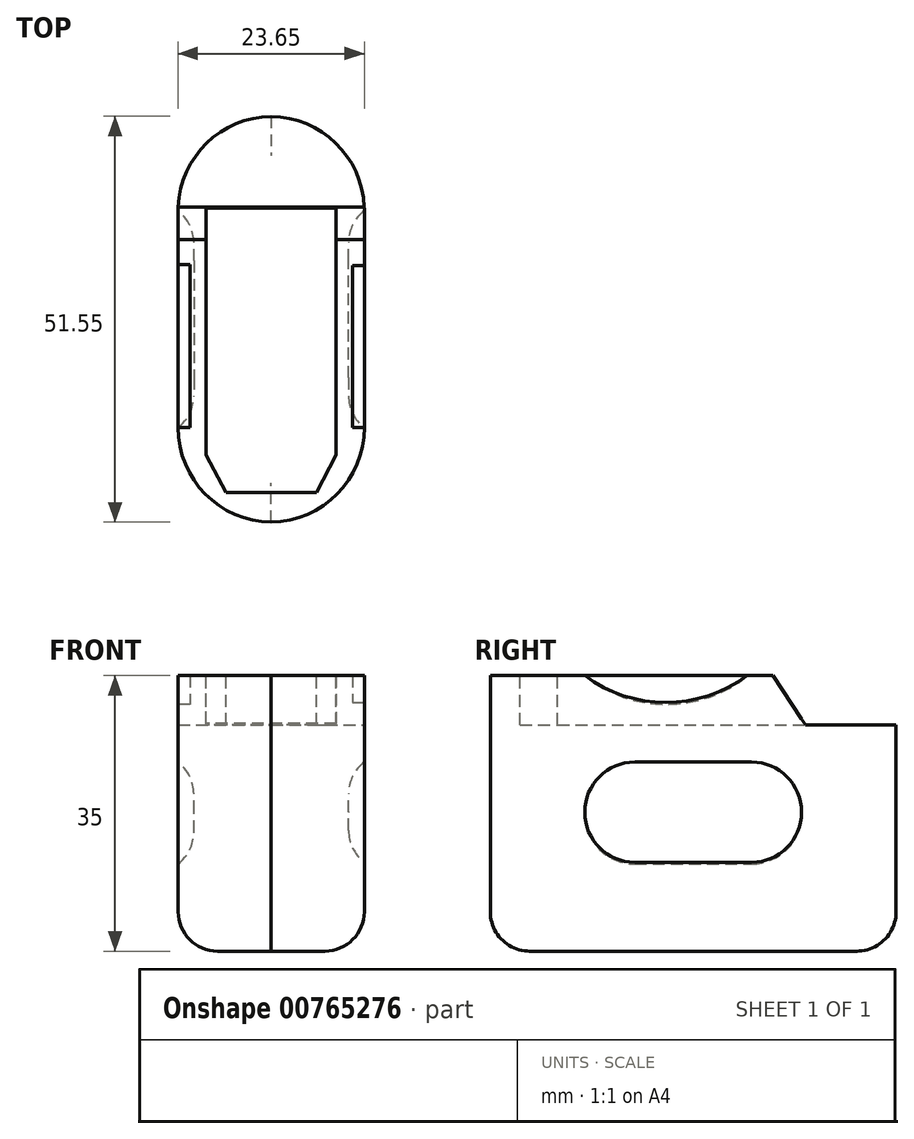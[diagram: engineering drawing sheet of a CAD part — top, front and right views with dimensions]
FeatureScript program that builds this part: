
annotation { "Feature Type Name" : "Feature", "Feature Type Description" : "" }
export const myFeature = defineFeature(function(context is Context, id is Id, definition is map)
    precondition{}
    {
        {
            var Q0;
            Q0=qCreatedBy(makeId("Top.planeOp"),FACE);
            var sketch = newSketch(context, id + "F0", { "sketchPlane" : qUnion([Q0])});
            skLineSegment(sketch, "E0", {"start": v(-11.06, 0) * mm, "end": v(-11.06, -51.55) * mm});
            skLineSegment(sketch, "E1", {"start": v(-11.06, -51.55) * mm, "end": v(12.59, -51.55) * mm});
            skLineSegment(sketch, "E2", {"start": v(12.59, -51.55) * mm, "end": v(12.59, 0) * mm});
            skLineSegment(sketch, "E3", {"start": v(-11.06, 0) * mm, "end": v(12.59, 0) * mm});
            skSolve(sketch);
        }
        {
            var Q0;
            Q0 = qSketchRegion(id + "F0", true);
            extrude(context, id + "F1", {"entities" : qUnion([Q0]), "depth" : 35 * mm, "offsetDistance" : 25.4 * mm});
        }
        {
            var Q0;
            Q0=makeQuery(id+"F1.opExtrude","SWEPT_FACE",FACE,{"disambiguationData":[OSD([sQuery(id+"F0.wireOp",EDGE,"E2")])]});
            var sketch = newSketch(context, id + "F2", { "sketchPlane" : qUnion([Q0])});
            skLineSegment(sketch, "E4", {"start": v(0, 35) * mm, "end": v(0, 28.75) * mm});
            skLineSegment(sketch, "E5", {"start": v(-11.5, 28.75) * mm, "end": v(-15.66, 35) * mm});
            skLineSegment(sketch, "E6", {"start": v(-11.5, 28.75) * mm, "end": v(0, 28.75) * mm});
            skLineSegment(sketch, "E7", {"start": v(0, 35) * mm, "end": v(-15.66, 35) * mm});
            skSolve(sketch);
        }
        {
            var Q0;
            Q0 = qSketchRegion(id + "F2", true);
            extrude(context, id + "F3", {"entities" : qUnion([Q0]), "operationType" : NewBodyOperationType.REMOVE, "endBound" : BoundingType.THROUGH_ALL, "oppositeDirection" : true, "depth" : 25.4 * mm, "offsetDistance" : 25.4 * mm});
        }
        {
            var Q0;
            Q0=makeQuery(id+"F1.opExtrude","CAP_FACE",FACE,{"disambiguationData":[OSD([sQuery(id+"F0.wireOp",EDGE,"E0"),sQuery(id+"F0.wireOp",EDGE,"E1"),sQuery(id+"F0.wireOp",EDGE,"E2"),sQuery(id+"F0.wireOp",EDGE,"E3")])],"isStart":false});
            var sketch = newSketch(context, id + "F4", { "sketchPlane" : qUnion([Q0])});
            skLineSegment(sketch, "E8", {"start": v(0.76, -47.76) * mm, "end": v(6.51, -47.76) * mm});
            skLineSegment(sketch, "E9.MirrorCS", {"start": v(0.76, -47.76) * mm, "end": v(-4.99, -47.76) * mm});
            skLineSegment(sketch, "E10", {"start": v(0.76, -15.66) * mm, "end": v(9.01, -15.66) * mm});
            skLineSegment(sketch, "E11", {"start": v(6.51, -47.76) * mm, "end": v(9.01, -43) * mm});
            skLineSegment(sketch, "E12", {"start": v(9.01, -43) * mm, "end": v(9.01, -15.66) * mm});
            skLineSegment(sketch, "E13.MirrorCS", {"start": v(-7.49, -43) * mm, "end": v(-7.49, -15.66) * mm});
            skLineSegment(sketch, "E14.MirrorCS", {"start": v(0.76, -15.66) * mm, "end": v(-7.49, -15.66) * mm});
            skLineSegment(sketch, "E15.MirrorCS", {"start": v(-4.99, -47.76) * mm, "end": v(-7.49, -43) * mm});
            skSolve(sketch);
        }
        {
            var Q0;
            Q0 = qSketchRegion(id + "F4", true);
            extrude(context, id + "F5", {"entities" : qUnion([Q0]), "operationType" : NewBodyOperationType.REMOVE, "oppositeDirection" : true, "depth" : 6.25 * mm, "offsetDistance" : 25.4 * mm});
        }
        {
            var Q0;
            Q0=makeQuery(id+"F1.opExtrude","CAP_FACE",FACE,{"disambiguationData":[OSD([sQuery(id+"F0.wireOp",EDGE,"E0"),sQuery(id+"F0.wireOp",EDGE,"E1"),sQuery(id+"F0.wireOp",EDGE,"E2"),sQuery(id+"F0.wireOp",EDGE,"E3")])],"isStart":false});
            var sketch = newSketch(context, id + "F6", { "sketchPlane" : qUnion([Q0])});
            skLineSegment(sketch, "E16", {"start": v(-7.49, -15.66) * mm, "end": v(9.01, -15.66) * mm});
            skLineSegment(sketch, "E17", {"start": v(9.01, -15.66) * mm, "end": v(9.01, -11.62) * mm});
            skLineSegment(sketch, "E18", {"start": v(9.01, -11.62) * mm, "end": v(-7.49, -11.62) * mm});
            skLineSegment(sketch, "E19", {"start": v(-7.49, -11.62) * mm, "end": v(-7.49, -15.66) * mm});
            skSolve(sketch);
        }
        {
            var Q0;
            Q0 = qSketchRegion(id + "F6", true);
            extrude(context, id + "F7", {"entities" : qUnion([Q0]), "operationType" : NewBodyOperationType.REMOVE, "oppositeDirection" : true, "depth" : 6.25 * mm, "offsetDistance" : 25.4 * mm});
        }
        {
            var Q0;
            Q0=makeQuery(id+"F1.opExtrude","SWEPT_EDGE",EDGE,{"disambiguationData":[OSD([sQuery(id+"F0.wireOp",EDGE,"E2"),sQuery(id+"F0.wireOp",EDGE,"E3")])]});
            var Q1;
            Q1=makeQuery(id+"F1.opExtrude","SWEPT_EDGE",EDGE,{"disambiguationData":[OSD([sQuery(id+"F0.wireOp",EDGE,"E0"),sQuery(id+"F0.wireOp",EDGE,"E3")])]});
            var Q2;
            Q2=makeQuery(id+"F1.opExtrude","SWEPT_EDGE",EDGE,{"disambiguationData":[OSD([sQuery(id+"F0.wireOp",EDGE,"E0"),sQuery(id+"F0.wireOp",EDGE,"E1")])]});
            var Q3;
            Q3=makeQuery(id+"F1.opExtrude","SWEPT_EDGE",EDGE,{"disambiguationData":[OSD([sQuery(id+"F0.wireOp",EDGE,"E1"),sQuery(id+"F0.wireOp",EDGE,"E2")])]});
            fillet(context, id + "F8", {"entities" : qUnion([Q0, Q1, Q2, Q3]), "radius" : 12 * mm, "tangentPropagation" : true, "allowEdgeOverflow" : false});
        }
        {
            var Q0;
            Q0=makeQuery(id+"F1.opExtrude","CAP_FACE",FACE,{"disambiguationData":[OSD([sQuery(id+"F0.wireOp",EDGE,"E0"),sQuery(id+"F0.wireOp",EDGE,"E1"),sQuery(id+"F0.wireOp",EDGE,"E2"),sQuery(id+"F0.wireOp",EDGE,"E3")])],"isStart":true});
            fillet(context, id + "F9", {"entities" : qUnion([Q0]), "radius" : 5 * mm, "tangentPropagation" : true, "allowEdgeOverflow" : false});
        }
        {
            var Q0;
            Q0=makeQuery(id+"F1.opExtrude","SWEPT_FACE",FACE,{"disambiguationData":[OSD([sQuery(id+"F0.wireOp",EDGE,"E2")])]});
            var sketch = newSketch(context, id + "F10", { "sketchPlane" : qUnion([Q0])});
            skLineSegment(sketch, "E20", {"start": v(-18.94, 35) * mm, "end": v(-39.55, 35) * mm});
            skArc(sketch, "E21", {"start": v(-39.55, 35) * mm, "mid": v(-29.24, 31.6) * mm, "end": v(-18.94, 35) * mm});
            skSolve(sketch);
        }
        {
            var Q0;
            Q0=makeQuery(id+"F1.opExtrude","SWEPT_FACE",FACE,{"disambiguationData":[OSD([sQuery(id+"F0.wireOp",EDGE,"E0")])]});
            var sketch = newSketch(context, id + "F11", { "sketchPlane" : qUnion([Q0])});
            skLineSegment(sketch, "E22", {"start": v(39.55, 35) * mm, "end": v(18.83, 35) * mm});
            skArc(sketch, "E23", {"start": v(18.83, 35) * mm, "mid": v(29.19, 31.34) * mm, "end": v(39.55, 35) * mm});
            skSolve(sketch);
        }
        {
            var Q0;
            Q0 = qSketchRegion(id + "F11", true);
            extrude(context, id + "F12", {"entities" : qUnion([Q0]), "operationType" : NewBodyOperationType.REMOVE, "oppositeDirection" : true, "depth" : 1.5 * mm, "offsetDistance" : 25.4 * mm});
        }
        {
            var Q0;
            Q0 = qSketchRegion(id + "F10", true);
            extrude(context, id + "F13", {"entities" : qUnion([Q0]), "operationType" : NewBodyOperationType.REMOVE, "oppositeDirection" : true, "depth" : 1.5 * mm, "offsetDistance" : 25.4 * mm});
        }
        {
            var Q0;
            Q0=makeQuery(id+"F1.opExtrude","SWEPT_FACE",FACE,{"disambiguationData":[OSD([sQuery(id+"F0.wireOp",EDGE,"E2")])]});
            var sketch = newSketch(context, id + "F14", { "sketchPlane" : qUnion([Q0])});
            skLineSegment(sketch, "E24", {"start": v(-25.78, 0) * mm, "end": v(-25.78, 35.31) * mm});
            skPoint(sketch, "E24.startSnap0", {"position": v(-25.78, 5) * mm});
            skLineSegment(sketch, "E25.bottom", {"start": v(-18.35, 11.3) * mm, "end": v(-33.2, 11.3) * mm});
            skLineSegment(sketch, "E25.top", {"start": v(-18.35, 24.01) * mm, "end": v(-33.2, 24.01) * mm});
            skLineSegment(sketch, "E25.left", {"start": v(-12, 17.65) * mm, "end": v(-12, 17.66) * mm});
            skLineSegment(sketch, "E25.right", {"start": v(-39.55, 17.65) * mm, "end": v(-39.55, 17.66) * mm});
            skPoint(sketch, "E25.middle", {"position": v(-25.78, 17.66) * mm});
            skPoint(sketch, "E26.visualSharp", {"position": v(-39.55, 24.01) * mm});
            skArc(sketch, "E26.filletArc", {"start": v(-33.2, 24.01) * mm, "mid": v(-37.7, 22.15) * mm, "end": v(-39.55, 17.66) * mm});
            skPoint(sketch, "E27.visualSharp", {"position": v(-12, 11.3) * mm});
            skArc(sketch, "E27.filletArc", {"start": v(-18.35, 11.3) * mm, "mid": v(-13.86, 13.16) * mm, "end": v(-12, 17.65) * mm});
            skPoint(sketch, "E28.visualSharp", {"position": v(-12, 24.01) * mm});
            skArc(sketch, "E28.filletArc", {"start": v(-12, 17.66) * mm, "mid": v(-13.86, 22.15) * mm, "end": v(-18.35, 24.01) * mm});
            skPoint(sketch, "E29.visualSharp", {"position": v(-39.55, 11.3) * mm});
            skArc(sketch, "E29.filletArc", {"start": v(-39.55, 17.65) * mm, "mid": v(-37.7, 13.16) * mm, "end": v(-33.2, 11.3) * mm});
            skSolve(sketch);
        }
        {
            var Q0;
            Q0 = qSketchRegion(id + "F14", true);
            extrude(context, id + "F15", {"entities" : qUnion([Q0]), "operationType" : NewBodyOperationType.REMOVE, "oppositeDirection" : true, "depth" : 2 * mm, "offsetDistance" : 25.4 * mm});
        }
        {
            var Q0;
            Q0=makeQuery(id+"F15.boolean.opBoolean","COPY",FACE,{"derivedFrom":makeQuery(id+"F15.opExtrude","CAP_FACE",FACE,{"disambiguationData":[OSD([sQuery(id+"F14.wireOp",EDGE,"E25.bottom"),sQuery(id+"F14.wireOp",EDGE,"E25.top"),sQuery(id+"F14.wireOp",EDGE,"E25.left"),sQuery(id+"F14.wireOp",EDGE,"E25.right"),sQuery(id+"F14.wireOp",EDGE,"E26.filletArc"),sQuery(id+"F14.wireOp",EDGE,"E27.filletArc"),sQuery(id+"F14.wireOp",EDGE,"E28.filletArc"),sQuery(id+"F14.wireOp",EDGE,"E29.filletArc")])],"isStart":false})});
            fillet(context, id + "F16", {"entities" : qUnion([Q0]), "radius" : 5.08 * mm, "tangentPropagation" : true, "allowEdgeOverflow" : false});
        }
        {
            var Q0;
            Q0=makeQuery(id+"F1.opExtrude","SWEPT_FACE",FACE,{"disambiguationData":[OSD([sQuery(id+"F0.wireOp",EDGE,"E0")])]});
            var sketch = newSketch(context, id + "F17", { "sketchPlane" : qUnion([Q0])});
            skLineSegment(sketch, "E30", {"start": v(25.78, 0) * mm, "end": v(25.78, 35.1) * mm});
            skPoint(sketch, "E30.startSnap0", {"position": v(25.78, 5) * mm});
            skLineSegment(sketch, "E31.bottom", {"start": v(33.2, 11.08) * mm, "end": v(18.35, 11.08) * mm});
            skLineSegment(sketch, "E31.top", {"start": v(33.2, 24.01) * mm, "end": v(18.35, 24.01) * mm});
            skLineSegment(sketch, "E31.left", {"start": v(39.55, 17.43) * mm, "end": v(39.55, 17.66) * mm});
            skLineSegment(sketch, "E31.right", {"start": v(12, 17.43) * mm, "end": v(12, 17.66) * mm});
            skPoint(sketch, "E31.middle", {"position": v(25.78, 17.55) * mm});
            skPoint(sketch, "E32.visualSharp", {"position": v(12, 24.01) * mm});
            skArc(sketch, "E32.filletArc", {"start": v(18.35, 24.01) * mm, "mid": v(13.86, 22.15) * mm, "end": v(12, 17.66) * mm});
            skPoint(sketch, "E33.visualSharp", {"position": v(39.55, 24.01) * mm});
            skArc(sketch, "E33.filletArc", {"start": v(39.55, 17.66) * mm, "mid": v(37.7, 22.15) * mm, "end": v(33.2, 24.01) * mm});
            skPoint(sketch, "E34.visualSharp", {"position": v(39.55, 11.08) * mm});
            skArc(sketch, "E34.filletArc", {"start": v(33.2, 11.08) * mm, "mid": v(37.7, 12.94) * mm, "end": v(39.55, 17.43) * mm});
            skPoint(sketch, "E35.visualSharp", {"position": v(12, 11.08) * mm});
            skArc(sketch, "E35.filletArc", {"start": v(12, 17.43) * mm, "mid": v(13.86, 12.94) * mm, "end": v(18.35, 11.08) * mm});
            skSolve(sketch);
        }
        {
            var Q0;
            Q0 = qSketchRegion(id + "F17", true);
            extrude(context, id + "F18", {"entities" : qUnion([Q0]), "operationType" : NewBodyOperationType.REMOVE, "depth" : 2 * mm, "offsetDistance" : 25.4 * mm});
        }
        {
            var Q0;
            Q0 = qSketchRegion(id + "F17", true);
            extrude(context, id + "F19", {"entities" : qUnion([Q0]), "operationType" : NewBodyOperationType.REMOVE, "oppositeDirection" : true, "depth" : 2 * mm, "offsetDistance" : 25.4 * mm});
        }
        {
            var Q0;
            Q0=makeQuery(id+"F19.boolean.opBoolean","COPY",FACE,{"derivedFrom":makeQuery(id+"F19.opExtrude","CAP_FACE",FACE,{"disambiguationData":[OSD([sQuery(id+"F17.wireOp",EDGE,"E31.bottom"),sQuery(id+"F17.wireOp",EDGE,"E31.top"),sQuery(id+"F17.wireOp",EDGE,"E31.left"),sQuery(id+"F17.wireOp",EDGE,"E31.right"),sQuery(id+"F17.wireOp",EDGE,"E32.filletArc"),sQuery(id+"F17.wireOp",EDGE,"E33.filletArc"),sQuery(id+"F17.wireOp",EDGE,"E34.filletArc"),sQuery(id+"F17.wireOp",EDGE,"E35.filletArc")])],"isStart":false})});
            fillet(context, id + "F20", {"entities" : qUnion([Q0]), "radius" : 5.08 * mm, "tangentPropagation" : true, "allowEdgeOverflow" : false});
        }
    });
